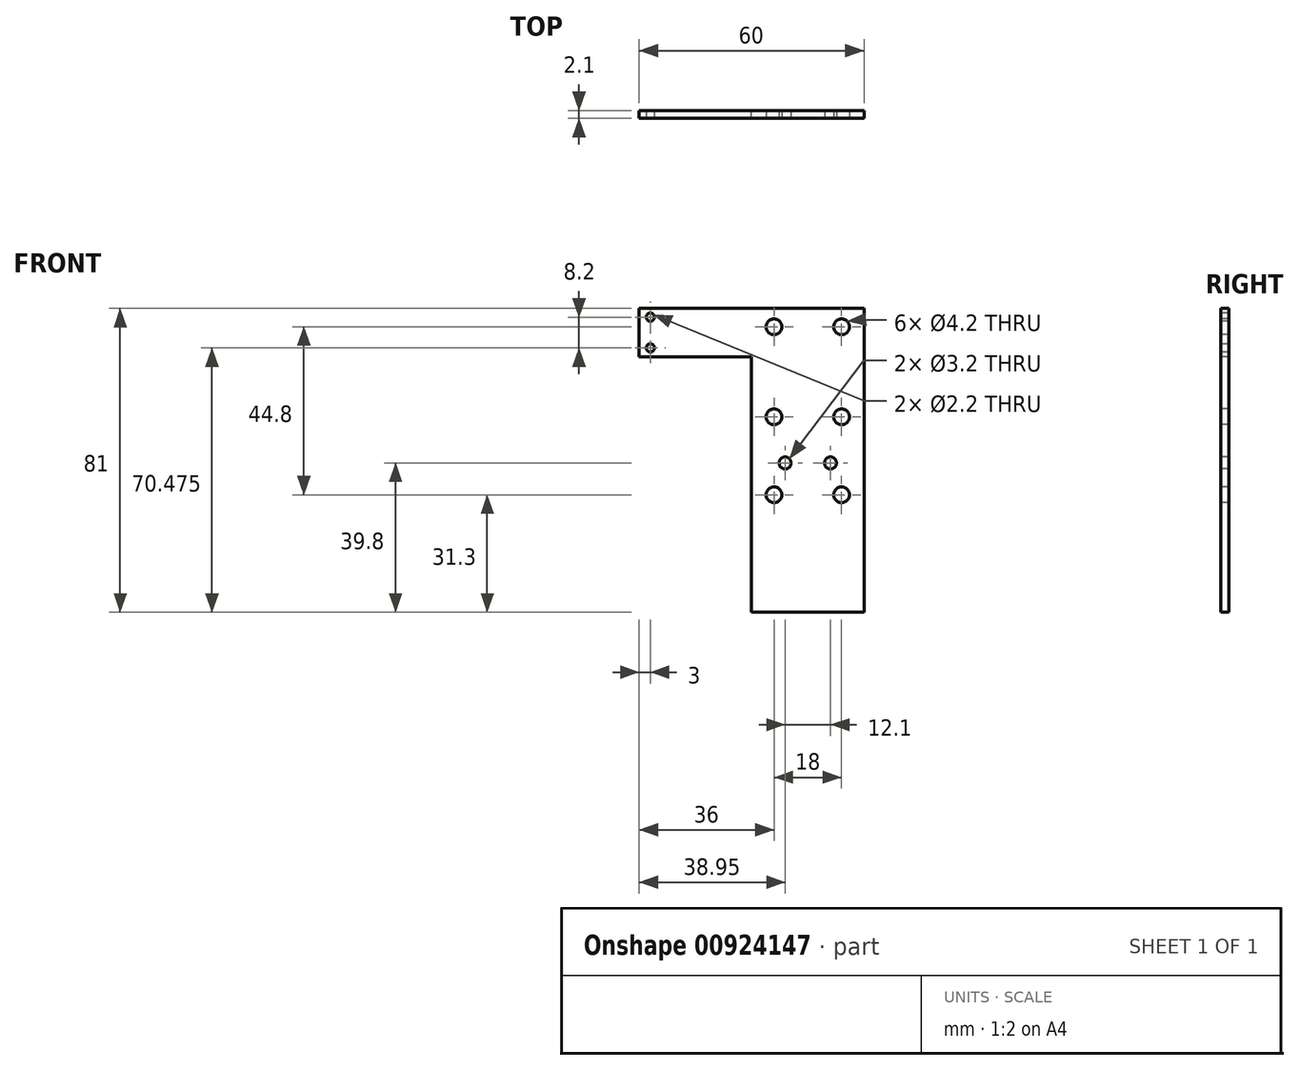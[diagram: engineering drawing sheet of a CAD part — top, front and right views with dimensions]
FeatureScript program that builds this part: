
annotation { "Feature Type Name" : "Feature", "Feature Type Description" : "" }
export const myFeature = defineFeature(function(context is Context, id is Id, definition is map)
    precondition{}
    {
        {
            var Q0;
            Q0=qCreatedBy(makeId("Front.planeOp"),FACE);
            var sketch = newSketch(context, id + "F0", { "sketchPlane" : qUnion([Q0])});
            skLineSegment(sketch, "E0.bottom", {"start": v(15, -40.5) * mm, "end": v(-15, -40.5) * mm});
            skLineSegment(sketch, "E0.top", {"start": v(15, 40.5) * mm, "end": v(-15, 40.5) * mm});
            skLineSegment(sketch, "E0.left", {"start": v(15, -40.5) * mm, "end": v(15, 40.5) * mm});
            skLineSegment(sketch, "E0.right", {"start": v(-15, -40.5) * mm, "end": v(-15, 40.5) * mm});
            skPoint(sketch, "E0.middle", {"position": v(0, 0) * mm});
            skSolve(sketch);
        }
        {
            var Q0;
            Q0=qSketchRegion(id+"F0",true);
            extrude(context, id + "F1", {"entities" : qUnion([Q0]), "offsetDistance" : 25 * mm, "depth" : 2.1 * mm});
        }
        {
            var Q0;
            Q0=makeQuery(id+"F1.opExtrude","CAP_FACE",FACE,{"disambiguationData":[OSD([sQuery(id+"F0.wireOp",EDGE,"E0.bottom"),sQuery(id+"F0.wireOp",EDGE,"E0.top"),sQuery(id+"F0.wireOp",EDGE,"E0.left"),sQuery(id+"F0.wireOp",EDGE,"E0.right")])],"isStart":false});
            var sketch = newSketch(context, id + "F2", { "sketchPlane" : qUnion([Q0])});
            skCircle(sketch, "E1", {"center": v(9, 35.6) * mm, "radius": 2.1 * mm});
            skCircle(sketch, "E2.0.1.0", {"center": v(9, 11.6) * mm, "radius": 2.1 * mm});
            skCircle(sketch, "E2.1.0.0", {"center": v(-9, 35.6) * mm, "radius": 2.1 * mm});
            skCircle(sketch, "E2.1.1.0", {"center": v(-9, 11.6) * mm, "radius": 2.1 * mm});
            skLineSegment(sketch, "E2.direction1", {"start": v(9, 35.6) * mm, "end": v(-9, 35.6) * mm, "construction": true});
            skLineSegment(sketch, "E2.direction2", {"start": v(9, 35.6) * mm, "end": v(9, 11.6) * mm, "construction": true});
            skCircle(sketch, "E3", {"center": v(9, -9.2) * mm, "radius": 2.1 * mm});
            skCircle(sketch, "E4.1.0.0", {"center": v(-9, -9.2) * mm, "radius": 2.1 * mm});
            skLineSegment(sketch, "E4.direction1", {"start": v(9, -9.2) * mm, "end": v(-9, -9.2) * mm, "construction": true});
            skCircle(sketch, "E5", {"center": v(6.05, -0.7) * mm, "radius": 1.6 * mm});
            skCircle(sketch, "E6", {"center": v(-6.05, -0.7) * mm, "radius": 1.6 * mm});
            skSolve(sketch);
        }
        {
            var Q0;
            Q0=qSketchRegion(id+"F2",true);
            extrude(context, id + "F3", {"entities" : qUnion([Q0]), "operationType" : NewBodyOperationType.REMOVE, "endBound" : BoundingType.THROUGH_ALL, "oppositeDirection" : true, "depth" : 25 * mm});
        }
        {
            var Q0;
            {var subQ0=sQuery(id+"F0.wireOp",EDGE,"E0.top");var subQ1=sQuery(id+"F0.wireOp",EDGE,"E0.right");Q0=makeQuery(id+"FvipgadzTs7h2ig_1.boolean.opBoolean","SPLIT",FACE,{"disambiguationData":[TD([makeQuery(id+"F1.opExtrude","SWEPT_FACE",FACE,{"disambiguationData":[OSD([subQ0])]})])],"derivedFrom":makeQuery(id+"F5f2Vist2cSmWYM_1.boolean.opBoolean","MERGE",FACE,{"derivedFrom":[makeQuery(id+"FH2s96wE7IiCr0O_1.boolean.opBoolean","MERGE",FACE,{"derivedFrom":[makeQuery(id+"FeYBOV7PRQpOrKr_1.boolean.opBoolean","MERGE",FACE,{"derivedFrom":[makeQuery(id+"F1.opExtrude","SWEPT_FACE",FACE,{"disambiguationData":[OSD([subQ1])]}),makeQuery(id+"FeYBOV7PRQpOrKr_1.opExtrude","SWEPT_FACE",FACE,{"disambiguationData":[OSD([sQuery(id+"Fsj7K8PfzOv52Cm_1.wireOp",EDGE,"jhQ0Sfq8-QwfK-1XKU-7ghn-kb5T5E4JH7wB.left")])]})]}),makeQuery(id+"FH2s96wE7IiCr0O_1.opExtrude","SWEPT_FACE",FACE,{"disambiguationData":[OSD([sQuery(id+"Fau4W2noinKfQj5_1.wireOp",EDGE,"tG47218x-zqqv-5zS3-eRtk-CQ31nMppaThV.left")])]})]}),makeQuery(id+"F5f2Vist2cSmWYM_1.opExtrude","SWEPT_FACE",FACE,{"disambiguationData":[OSD([sQuery(id+"F0SI9y80Xgv7Qnx_1.wireOp",EDGE,"MZaP7wyF-QaMZ-VxLV-YAOh-EydADYJaR9qK.left")])]})]})});}
            var sketch = newSketch(context, id + "F4", { "sketchPlane" : qUnion([Q0])});
            skLineSegment(sketch, "E7.bottom", {"start": v(0, 40.5) * mm, "end": v(2.1, 40.5) * mm});
            skLineSegment(sketch, "E7.top", {"start": v(0, 27.65) * mm, "end": v(2.1, 27.65) * mm});
            skLineSegment(sketch, "E7.left", {"start": v(0, 40.5) * mm, "end": v(0, 27.65) * mm});
            skLineSegment(sketch, "E7.right", {"start": v(2.1, 40.5) * mm, "end": v(2.1, 27.65) * mm});
            skSolve(sketch);
        }
        {
            var Q0;
            Q0=qSketchRegion(id+"F4",true);
            extrude(context, id + "F5", {"entities" : qUnion([Q0]), "operationType" : NewBodyOperationType.ADD, "depth" : 30 * mm, "offsetDistance" : 25 * mm});
        }
        {
            var Q0;
            Q0=makeQuery(id+"F5.boolean.opBoolean","MERGE",FACE,{"derivedFrom":[makeQuery(id+"F1.opExtrude","CAP_FACE",FACE,{"disambiguationData":[OSD([sQuery(id+"F0.wireOp",EDGE,"E0.bottom"),sQuery(id+"F0.wireOp",EDGE,"E0.top"),sQuery(id+"F0.wireOp",EDGE,"E0.left"),sQuery(id+"F0.wireOp",EDGE,"E0.right")])],"isStart":false}),makeQuery(id+"F5.opExtrude","SWEPT_FACE",FACE,{"disambiguationData":[OSD([sQuery(id+"F4.wireOp",EDGE,"E7.right")])]})]});
            var sketch = newSketch(context, id + "F6", { "sketchPlane" : qUnion([Q0])});
            skCircle(sketch, "E8", {"center": v(-42, 38.17) * mm, "radius": 1.1 * mm});
            skCircle(sketch, "E9", {"center": v(-42, 29.97) * mm, "radius": 1.1 * mm});
            skLineSegment(sketch, "E10", {"start": v(-45, 34.08) * mm, "end": v(-26.44, 34.08) * mm});
            skSolve(sketch);
        }
        {
            var Q0;
            Q0=makeQuery(id+"F6.imprint","IMPRINT",FACE,{"disambiguationData":[TD([[makeQuery(id+"F6.imprint","IMPRINT",EDGE,{"derivedFrom":sQuery(id+"F6.wireOp",EDGE,"E8")}),1.0]])]});
            var Q1;
            Q1=makeQuery(id+"F6.imprint","IMPRINT",FACE,{"disambiguationData":[TD([[makeQuery(id+"F6.imprint","IMPRINT",EDGE,{"derivedFrom":sQuery(id+"F6.wireOp",EDGE,"E9")}),1.0]])]});
            extrude(context, id + "F7", {"entities" : qUnion([Q0, Q1]), "operationType" : NewBodyOperationType.REMOVE, "oppositeDirection" : true, "depth" : 25 * mm, "offsetDistance" : 25 * mm});
        }
    });
